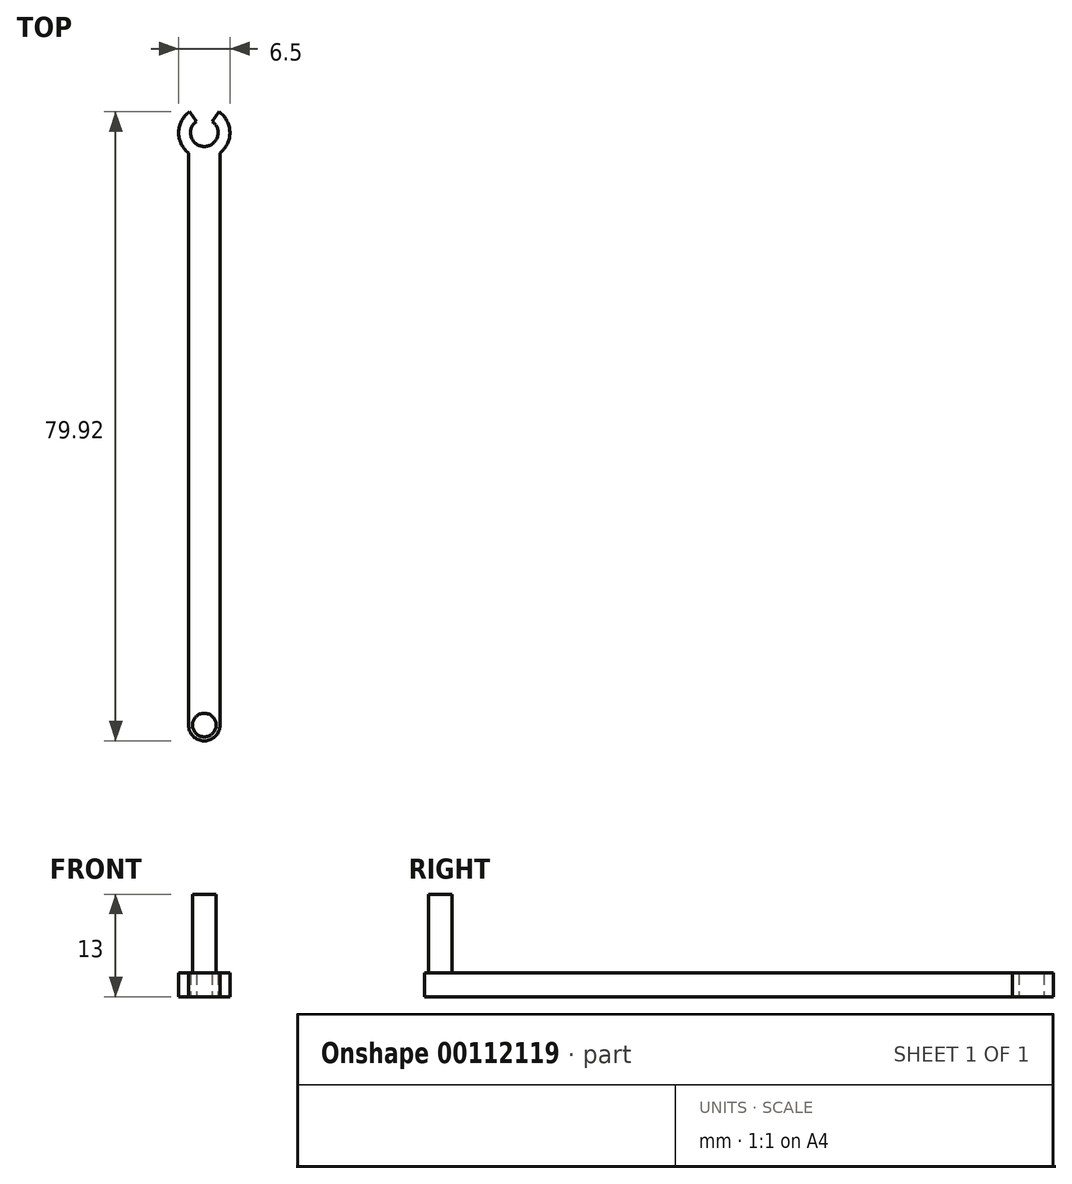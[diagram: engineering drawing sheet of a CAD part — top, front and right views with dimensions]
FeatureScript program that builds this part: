
annotation { "Feature Type Name" : "Feature", "Feature Type Description" : "" }
export const myFeature = defineFeature(function(context is Context, id is Id, definition is map)
    precondition{}
    {
        {
            var Q0;
            Q0=qCreatedBy(makeId("Top.planeOp"),FACE);
            var sketch = newSketch(context, id + "F0", { "sketchPlane" : qUnion([Q0])});
            skArc(sketch, "E0", {"start": v(1.4, 80.84) * mm, "mid": v(3.25, 74.92) * mm, "end": v(5.1, 80.84) * mm});
            skPoint(sketch, "E0.centerSnap0", {"position": v(3.25, 81.42) * mm});
            skArc(sketch, "E1", {"start": v(2.25, 79.61) * mm, "mid": v(3.25, 76.42) * mm, "end": v(4.25, 79.61) * mm});
            skLineSegment(sketch, "E2", {"start": v(3.25, 78.17) * mm, "end": v(5.1, 80.84) * mm});
            skLineSegment(sketch, "E3", {"start": v(3.25, 78.17) * mm, "end": v(1.4, 80.84) * mm});
            skLineSegment(sketch, "E4", {"start": v(2.25, 79.61) * mm, "end": v(4.25, 79.61) * mm});
            skLineSegment(sketch, "E5", {"start": v(3.25, 81.42) * mm, "end": v(3.25, 78.17) * mm});
            skLineSegment(sketch, "E6", {"start": v(3.25, 74.92) * mm, "end": v(3.25, 0.92) * mm});
            skLineSegment(sketch, "E7", {"start": v(1.25, 75.61) * mm, "end": v(1.25, 2.92) * mm});
            skLineSegment(sketch, "E8", {"start": v(5.25, 75.61) * mm, "end": v(5.25, 2.92) * mm});
            skPoint(sketch, "E9.orphan", {"position": v(0, 81.42) * mm});
            skPoint(sketch, "E10.trimOffspring.end.orphan", {"position": v(6.5, 81.42) * mm});
            skCircle(sketch, "E11", {"center": v(3.25, 2.92) * mm, "radius": 2 * mm});
            skSolve(sketch);
        }
        {
            var Q0;
            {var subQ1=sQuery(id+"F0.wireOp",EDGE,"7RT2il7h-merz-ThkM-nwO2-sf328oHhcdXs");var subQ7=makeQuery(id+"F0.imprint","INTERSECT",VERTEX,{"derivedFrom":[subQ1,sQuery(id+"F0.wireOp",EDGE,"E6")]});Q0=makeQuery(id+"F0.imprint","IMPRINT",FACE,{"disambiguationData":[TD([[makeQuery(id+"F0.imprint","IMPRINT",EDGE,{"disambiguationData":[TD([[subQ7,1.0]])],"derivedFrom":subQ1}),1.0]])]});}
            var Q1;
            {var subQ0=sQuery(id+"F0.wireOp",EDGE,"E6");Q1=makeQuery(id+"F0.imprint","IMPRINT",FACE,{"disambiguationData":[TD([[makeQuery(id+"F0.imprint","IMPRINT",EDGE,{"derivedFrom":subQ0}),-1.0]])]});}
            var Q2;
            {var subQ0=sQuery(id+"F0.wireOp",EDGE,"E6");Q2=makeQuery(id+"F0.imprint","IMPRINT",FACE,{"disambiguationData":[TD([[makeQuery(id+"F0.imprint","IMPRINT",EDGE,{"derivedFrom":subQ0}),1.0]])]});}
            var Q3;
            {var subQ8=sQuery(id+"F0.wireOp",EDGE,"E1");Q3=makeQuery(id+"F0.imprint","IMPRINT",FACE,{"disambiguationData":[TD([[makeQuery(id+"F0.imprint","IMPRINT",EDGE,{"derivedFrom":subQ8}),-1.0]])]});}
            var Q4;
            {var subQ3=sQuery(id+"F0.wireOp",EDGE,"E7");Q4=makeQuery(id+"F0.imprint","IMPRINT",FACE,{"disambiguationData":[TD([[makeQuery(id+"F0.imprint","IMPRINT",EDGE,{"derivedFrom":subQ3}),1.0]])]});}
            var Q5;
            {var subQ3=sQuery(id+"F0.wireOp",EDGE,"E8");Q5=makeQuery(id+"F0.imprint","IMPRINT",FACE,{"disambiguationData":[TD([[makeQuery(id+"F0.imprint","IMPRINT",EDGE,{"derivedFrom":subQ3}),-1.0]])]});}
            extrude(context, id + "F1", {"entities" : qUnion([Q0, Q1, Q2, Q3, Q4, Q5]), "depth" : 3 * mm});
        }
        {
            var Q0;
            Q0=makeQuery(id+"F1.opExtrude","CAP_FACE",FACE,{"disambiguationData":[OSD([sQuery(id+"F0.wireOp",EDGE,"E0"),sQuery(id+"F0.wireOp",EDGE,"E1"),sQuery(id+"F0.wireOp",EDGE,"E2"),sQuery(id+"F0.wireOp",EDGE,"E3"),sQuery(id+"F0.wireOp",EDGE,"E7"),sQuery(id+"F0.wireOp",EDGE,"E8"),sQuery(id+"F0.wireOp",EDGE,"E11")])],"isStart":false});
            var sketch = newSketch(context, id + "F2", { "sketchPlane" : qUnion([Q0])});
            skArc(sketch, "E12.0", {"start": v(1.25, 2.92) * mm, "mid": v(3.25, 0.92) * mm, "end": v(5.25, 2.92) * mm});
            skCircle(sketch, "E13", {"center": v(3.25, 2.92) * mm, "radius": 1.5 * mm});
            skSolve(sketch);
        }
        {
            var Q0;
            Q0 = qSketchRegion(id + "F2", true);
            extrude(context, id + "F3", {"entities" : qUnion([Q0]), "operationType" : NewBodyOperationType.ADD, "depth" : 10 * mm});
        }
    });
